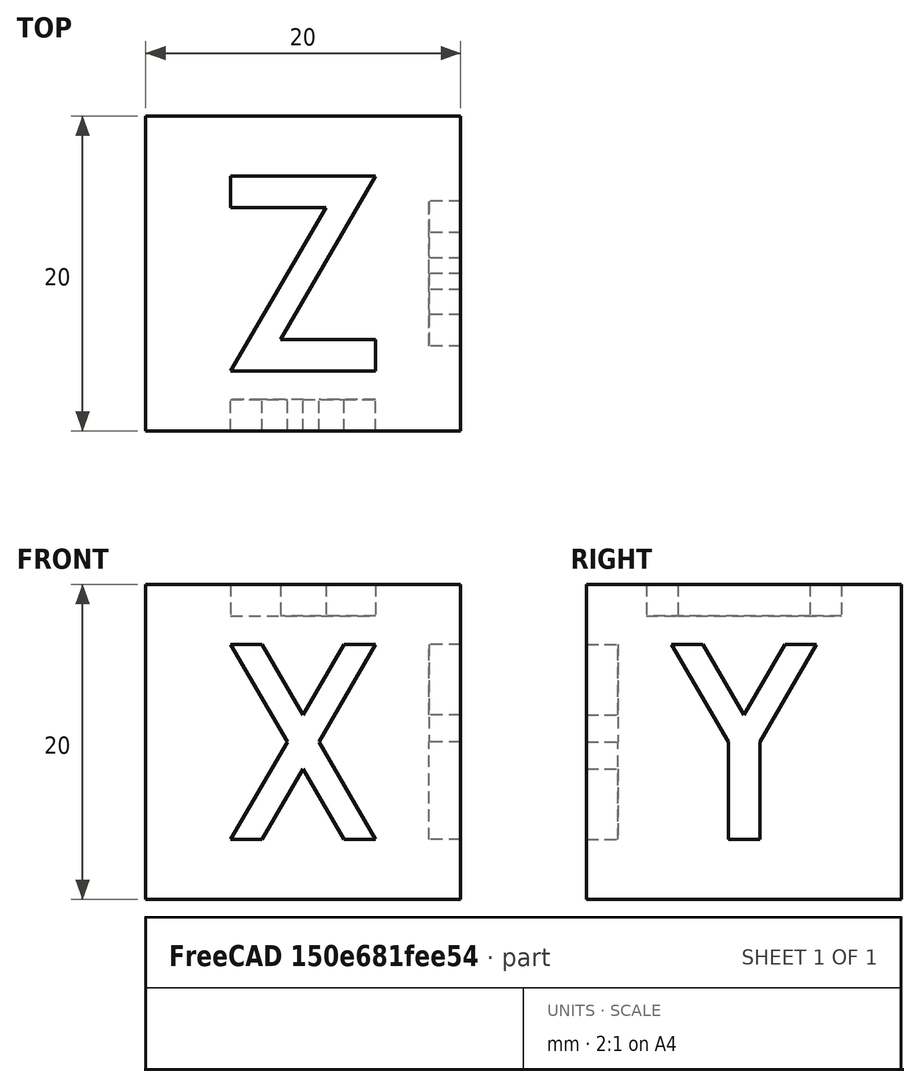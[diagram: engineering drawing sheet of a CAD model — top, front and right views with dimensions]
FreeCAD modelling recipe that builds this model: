
FCSTD DOCUMENT  (FreeCAD 0.19R24366 (Git))
Label: XYZ-Cube
Comment: FreeCAD-models by mgesteiro -- https://github.com/mgesteiro/FreeCAD-models
License: Creative Commons Attribution-ShareAlike
LicenseURL: http://creativecommons.org/licenses/by-sa/4.0/
objects: Sketcher::SketchObject×4, PartDesign::Pocket×3, Mesh::Feature×1, PartDesign::Pad×1, PartDesign::Body×1
note: 13 computed .brp shape members not serialized (recipe doc carries the construction recipe); baked Part::Feature solids carry a one-line shape summary decoded from their .brp

FEATURE [Mesh::Feature] xyzCalibration_cube  label="xyzCalibration_cube-original"
FEATURE [Sketcher::SketchObject] Sketch
  FullyConstrained = true
  MapMode = 5
  Support = -> [XY_Plane]
  sketch-geometry (4):
    g0: LineSegment StartX=0 StartY=0 StartZ=0 EndX=20 EndY=0 EndZ=0
    g1: LineSegment StartX=20 StartY=0 StartZ=0 EndX=20 EndY=20 EndZ=0
    g2: LineSegment StartX=20 StartY=20 StartZ=0 EndX=0 EndY=20 EndZ=0
    g3: LineSegment StartX=0 StartY=20 StartZ=0 EndX=0 EndY=0 EndZ=0
  constraints (11):
    c: Coincident(g0,g1)
    c: Coincident(g1,g2)
    c: Coincident(g2,g3)
    c: Coincident(g3,g0)
    c: Horizontal(g0)
    c: Horizontal(g2)
    c: Vertical(g1)
    c: Vertical(g3)
    c: Coincident(g0,g-1)
    c: Equal(g2,g1)
    c: DistanceX(g2,g2) = 20
FEATURE [PartDesign::Pad] Pad
  Direction = (1,1,1)
  Length = 20
  Length2 = 100
  Profile = -> Sketch
  Type = 0
FEATURE [Sketcher::SketchObject] Sketch001  label="Sketch-X"
  FullyConstrained = true
  MapMode = 5
  Placement = pos=(0,0,0) rot=(1,0,0;1.5708rad)
  Support = -> [Pad]
  sketch-geometry (16):
    g0: LineSegment StartX=5.4 StartY=16.2 StartZ=0 EndX=9 EndY=10 EndZ=0
    g1: LineSegment StartX=12.6 StartY=3.8 StartZ=0 EndX=14.6 EndY=3.8 EndZ=0
    g2: LineSegment StartX=14.6 StartY=3.8 StartZ=0 EndX=11 EndY=10 EndZ=0
    g3: LineSegment StartX=7.4 StartY=16.2 StartZ=0 EndX=5.4 EndY=16.2 EndZ=0
    g4: LineSegment StartX=12.6 StartY=16.2 StartZ=0 EndX=14.6 EndY=16.2 EndZ=0
    g5: LineSegment StartX=14.6 StartY=16.2 StartZ=0 EndX=11 EndY=10 EndZ=0
    g6: LineSegment StartX=7.4 StartY=3.8 StartZ=0 EndX=5.4 EndY=3.8 EndZ=0
    g7: LineSegment StartX=5.4 StartY=3.8 StartZ=0 EndX=9 EndY=10 EndZ=0
    g8: LineSegment StartX=5.4 StartY=16.2 StartZ=0 EndX=14.6 EndY=16.2 EndZ=0
    g9: LineSegment StartX=14.6 StartY=16.2 StartZ=0 EndX=14.6 EndY=3.8 EndZ=0
    g10: LineSegment StartX=14.6 StartY=3.8 StartZ=0 EndX=5.4 EndY=3.8 EndZ=0
    g11: LineSegment StartX=5.4 StartY=3.8 StartZ=0 EndX=5.4 EndY=16.2 EndZ=0
    g12: LineSegment StartX=10 StartY=11.7222 StartZ=0 EndX=12.6 EndY=16.2 EndZ=0
    g13: LineSegment StartX=10 StartY=8.27778 StartZ=0 EndX=7.4 EndY=3.8 EndZ=0
    g14: LineSegment StartX=10 StartY=11.7222 StartZ=0 EndX=7.4 EndY=16.2 EndZ=0
    g15: LineSegment StartX=10 StartY=8.27778 StartZ=0 EndX=12.6 EndY=3.8 EndZ=0
  constraints (40):
    c: Coincident(g15,g1)
    c: Horizontal(g1)
    c: Coincident(g1,g2)
    c: Coincident(g14,g3)
    c: Coincident(g3,g0)
    c: Horizontal(g4)
    c: Coincident(g4,g5)
    c: Coincident(g13,g6)
    c: Horizontal(g6)
    c: Coincident(g6,g7)
    c: Coincident(g12,g4)
    c: Equal(g6,g1)
    c: Equal(g1,g4)
    c: Equal(g4,g3)
    c: Horizontal(g3)
    c: Coincident(g8,g9)
    c: Coincident(g9,g10)
    c: Coincident(g10,g11)
    c: Coincident(g11,g8)
    c: Horizontal(g8)
    c: Horizontal(g10)
    c: Vertical(g9)
    c: Vertical(g11)
    c: Coincident(g8,g0)
    c: Coincident(g9,g1)
    c: Coincident(g4,g8)
    c: Coincident(g10,g6)
    c: DistanceX(g1,g1) = 2
    c: DistanceX(g10,g10) = 9.2
    c: DistanceY(g9,g9) = 12.4
    c: DistanceX(g6) = 5.4
    c: DistanceY(g6) = 3.8
    c: Tangent(g7,g12)
    c: Tangent(g5,g13)
    c: Coincident(g2,g5)
    c: Coincident(g14,g12)
    c: Tangent(g2,g14)
    c: Coincident(g0,g7)
    c: Coincident(g15,g13)
    c: Tangent(g0,g15)
FEATURE [PartDesign::Pocket] Pocket  label="Pocket-X"
  BaseFeature = -> Pad
  Length = 2
  Length2 = 100
  Profile = -> Sketch001
  Type = 0
FEATURE [Sketcher::SketchObject] Sketch002  label="Sketch-Y"
  FullyConstrained = true
  MapMode = 5
  Placement = pos=(20,0,0) rot=(0.57735,0.57735,0.57735;2.0944rad)
  Support = -> [Pad]
  sketch-geometry (15):
    g0: LineSegment StartX=5.4 StartY=16.2 StartZ=0 EndX=9 EndY=10 EndZ=0
    g1: LineSegment StartX=7.4 StartY=16.2 StartZ=0 EndX=5.4 EndY=16.2 EndZ=0
    g2: LineSegment StartX=12.6 StartY=16.2 StartZ=0 EndX=14.6 EndY=16.2 EndZ=0
    g3: LineSegment StartX=14.6 StartY=16.2 StartZ=0 EndX=11 EndY=10 EndZ=0
    g4: LineSegment StartX=5.4 StartY=16.2 StartZ=0 EndX=14.6 EndY=16.2 EndZ=0
    g5: LineSegment StartX=14.6 StartY=16.2 StartZ=0 EndX=14.6 EndY=3.8 EndZ=0
    g6: LineSegment StartX=14.6 StartY=3.8 StartZ=0 EndX=5.4 EndY=3.8 EndZ=0
    g7: LineSegment StartX=5.4 StartY=3.8 StartZ=0 EndX=5.4 EndY=16.2 EndZ=0
    g8: LineSegment StartX=10 StartY=11.7222 StartZ=0 EndX=12.6 EndY=16.2 EndZ=0
    g9: LineSegment StartX=10 StartY=11.7222 StartZ=0 EndX=7.4 EndY=16.2 EndZ=0
    g10: LineSegment StartX=9 StartY=10 StartZ=0 EndX=9 EndY=3.8 EndZ=0
    g11: LineSegment StartX=9 StartY=3.8 StartZ=0 EndX=11 EndY=3.8 EndZ=0
    g12: LineSegment StartX=11 StartY=3.8 StartZ=0 EndX=11 EndY=10 EndZ=0
    g13: LineSegment StartX=12.6 StartY=16.2 StartZ=0 EndX=5.4 EndY=3.8 EndZ=0
    g14: LineSegment StartX=7.4 StartY=16.2 StartZ=0 EndX=14.6 EndY=3.8 EndZ=0
  constraints (41):
    c: Coincident(g9,g1)
    c: Coincident(g1,g0)
    c: Horizontal(g2)
    c: Coincident(g2,g3)
    c: Coincident(g8,g2)
    c: Equal(g2,g1)
    c: Horizontal(g1)
    c: Coincident(g4,g5)
    c: Coincident(g5,g6)
    c: Coincident(g6,g7)
    c: Coincident(g7,g4)
    c: Horizontal(g4)
    c: Horizontal(g6)
    c: Vertical(g5)
    c: Vertical(g7)
    c: Coincident(g4,g0)
    c: Coincident(g2,g4)
    c: DistanceX(g6,g6) = 9.2
    c: DistanceY(g5,g5) = 12.4
    c: DistanceX(g6) = 5.4
    c: DistanceY(g6) = 3.8
    c: Coincident(g9,g8)
    c: DistanceX(g2,g2) = 2
    c: Coincident(g0,g10)
    c: PointOnObject(g10,g6)
    c: Vertical(g10)
    c: Coincident(g10,g11)
    c: PointOnObject(g11,g6)
    c: Coincident(g11,g12)
    c: Coincident(g12,g3)
    c: Vertical(g12)
    c: Coincident(g13,g2)
    c: Coincident(g13,g6)
    c: Coincident(g14,g1)
    c: Coincident(g14,g5)
    c: PointOnObject(g8,g13)
    c: PointOnObject(g8,g14)
    c: Parallel(g8,g3)
    c: Parallel(g9,g0)
    c: Equal(g11,g2)
    c: Horizontal(g0,g3)
FEATURE [PartDesign::Pocket] Pocket001  label="Pocket-Y"
  BaseFeature = -> Pocket
  Length = 2
  Length2 = 100
  Profile = -> Sketch002
  Type = 0
FEATURE [Sketcher::SketchObject] Sketch003  label="Sketch-Z"
  FullyConstrained = true
  MapMode = 5
  Placement = pos=(0,0,20) rot=(0,0,1;0rad)
  Support = -> [Pad]
  sketch-geometry (14):
    g0: LineSegment StartX=5.4 StartY=16.2 StartZ=0 EndX=14.6 EndY=16.2 EndZ=0
    g1: LineSegment StartX=14.6 StartY=16.2 StartZ=0 EndX=14.6 EndY=3.8 EndZ=0
    g2: LineSegment StartX=14.6 StartY=3.8 StartZ=0 EndX=5.4 EndY=3.8 EndZ=0
    g3: LineSegment StartX=5.4 StartY=3.8 StartZ=0 EndX=5.4 EndY=16.2 EndZ=0
    g4: LineSegment StartX=12.6 StartY=16.2 StartZ=0 EndX=5.4 EndY=3.8 EndZ=0
    g5: LineSegment StartX=14.6 StartY=16.2 StartZ=0 EndX=7.4 EndY=3.8 EndZ=0
    g6: LineSegment StartX=5.4 StartY=16.2 StartZ=0 EndX=5.4 EndY=14.2 EndZ=0
    g7: LineSegment StartX=5.4 StartY=14.2 StartZ=0 EndX=11.4387 EndY=14.2 EndZ=0
    g8: LineSegment StartX=11.4387 StartY=14.2 StartZ=0 EndX=5.4 EndY=3.8 EndZ=0
    g9: LineSegment StartX=5.4 StartY=3.8 StartZ=0 EndX=14.6 EndY=3.8 EndZ=0
    g10: LineSegment StartX=14.6 StartY=3.8 StartZ=0 EndX=14.6 EndY=5.8 EndZ=0
    g11: LineSegment StartX=14.6 StartY=5.8 StartZ=0 EndX=8.56129 EndY=5.8 EndZ=0
    g12: LineSegment StartX=8.56129 StartY=5.8 StartZ=0 EndX=14.6 EndY=16.2 EndZ=0
    g13: LineSegment StartX=5.4 StartY=16.2 StartZ=0 EndX=14.6 EndY=16.2 EndZ=0
  constraints (38):
    c: Coincident(g0,g1)
    c: Coincident(g1,g2)
    c: Coincident(g2,g3)
    c: Coincident(g3,g0)
    c: Horizontal(g0)
    c: Horizontal(g2)
    c: Vertical(g1)
    c: Vertical(g3)
    c: DistanceX(g2,g2) = 9.2
    c: DistanceY(g1,g1) = 12.4
    c: DistanceX(g2) = 5.4
    c: DistanceY(g2) = 3.8
    c: DistanceX(g4,g0) = 2
    c: Coincident(g4,g2)
    c: PointOnObject(g5,g2)
    c: Parallel(g5,g4)
    c: Coincident(g0,g6)
    c: PointOnObject(g6,g3)
    c: Coincident(g6,g7)
    c: PointOnObject(g7,g4)
    c: Horizontal(g7)
    c: Coincident(g7,g8)
    c: Coincident(g8,g2)
    c: Coincident(g8,g9)
    c: Coincident(g9,g1)
    c: Coincident(g9,g10)
    c: PointOnObject(g10,g1)
    c: Coincident(g10,g11)
    c: Horizontal(g11)
    c: Coincident(g11,g12)
    c: Coincident(g5,g0)
    c: Coincident(g12,g0)
    c: PointOnObject(g4,g0)
    c: PointOnObject(g11,g5)
    c: Equal(g6,g10)
    c: DistanceY(g6,g6) = 2
    c: Coincident(g13,g6)
    c: Coincident(g13,g12)
FEATURE [PartDesign::Pocket] Pocket002  label="Pocket-Z"
  BaseFeature = -> Pocket001
  Length = 2
  Length2 = 100
  Profile = -> Sketch003
  Type = 0
FEATURE [PartDesign::Body] Body
  Group = -> [Sketch,Pad,Sketch001,Pocket,Sketch002,Pocket001,Sketch003,Pocket002]
  Origin = -> Origin
  Tip = -> Pocket002
